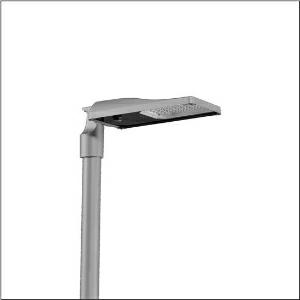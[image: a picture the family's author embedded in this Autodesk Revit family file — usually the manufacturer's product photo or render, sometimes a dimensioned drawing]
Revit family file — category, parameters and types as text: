
# Revit family: streetlight_sl_31_mini___st1_0a_5xh2d3ar08ja_7f0c
name_source: partatom
category: Lighting Fixtures
units: mm (PartAtom-declared; Revit-internal decimal feet)

## family parameters
Cut with Voids When Loaded = No
Host = Face
Light Source = No
Part Type = Normal
Room Calculation Point = No
Round Connector Dimension = Use Diameter
Shared = No

## types (1)
- --- (1 x LED, 12270 lm, 82.5 W, 3000K)
    Apparent Load = 83 VA
    CIE Flux Codes = 40 73 97 100 100
    Color Rendering = 70
    Color Temperature = 3000K
    Default Elevation = 1800 mm
    Description = Streetlight SL 31 mini D4i mast luminaire for post-top, side-entry; light control with lens of PMMA; light distribution: ST1.0a, direct asymmetric distribution, for standard-compliant lighting for roads and squares; LED: luminous flux: 12.270lm, light colour: 730, colour temperature: 3000K; luminous efficacy: 148,7lm/W; control: pre-setting: logarithmic dimming characteristic, flexible luminous flux parameterisation, time-dependent luminous flux control, constant luminous flux control, power reduction, intelligent temperature release in ECG and LED module, overheat protection; luminaire housing, of diecast aluminium, SITECO metallic grey (DB 702S), corrosivity category C5 high according to DIN EN ISO 12944; cover of toughened safety glass, transparent, mast flange of diecast aluminium, SITECO metallic grey (DB 702S), spigot size: 76/60mm, mast flange included unmounted; cable length: 10,5m, connection cable pre-assembled; mains connection: 220..240V, AC, 50/60Hz; power consumption (at start of service life): 82,5W / (at end of service life): 90,1W / (with reduced operation 50%): 36,8W; protection rating (complete): IP66; insulation class (complete): insulation class II (safety insulation); impact resistance: IK09; certification: CE, ENEC, ENEC+, VDE, UKCA, ZD4i; permissible operating ambient temperature for outdoor applications: -40..+50°C; packaging unit: 1 piece

Light Distribution: ST1.0a
    Height = 76 mm
    Lamp = 1 x LED
    Lamp Light Flux = 12270 lm
    Lamp Power = 82.5 W
    Lamp count = 1
    Length = 547 mm
    Luminous efficacy = 149 lm/W
    Manufacturer = Siteco
    ModVariant = No
    Model = 5XH2D3AR08JA
    Number of Poles = 1
    OnlyDefault = Yes
    Power Factor = 1
    Product Name = Streetlight SL 31 mini | ST1.0a
    Product group = mast luminaire | pylon top
    ProductGroupID = 6100
    Protection Class = Protection class II
    Protection Degree = IP 66
    RLX_Detail_Level = 1
    RLX_Emergency_Light_Flux = 0 lm
    RLX_Emergency_Type = 0
    RLX_Emergency_Type_DB = No
    RlxData = <blob elided: 39685 chars, md5=de982fef>
    Socket = socket
    Standby Power = 0 W
    System Light Flux = 12270 lm
    System Power = 83 W
    Type Comments = factory setting: luminous flux: 100 % | dim-lin: 254 | 870 mA
    Type Image = l_1300328.jpg
    URL = http://relux.com
    VarID = @adj_057755
    Voltage = 0 V
    Weight = 0.00 kg
    Width = 265 mm

## geometry (parser evidence)
native form markers: Blend x4, Sweep x10
no freeform markers — native parametric forms only
